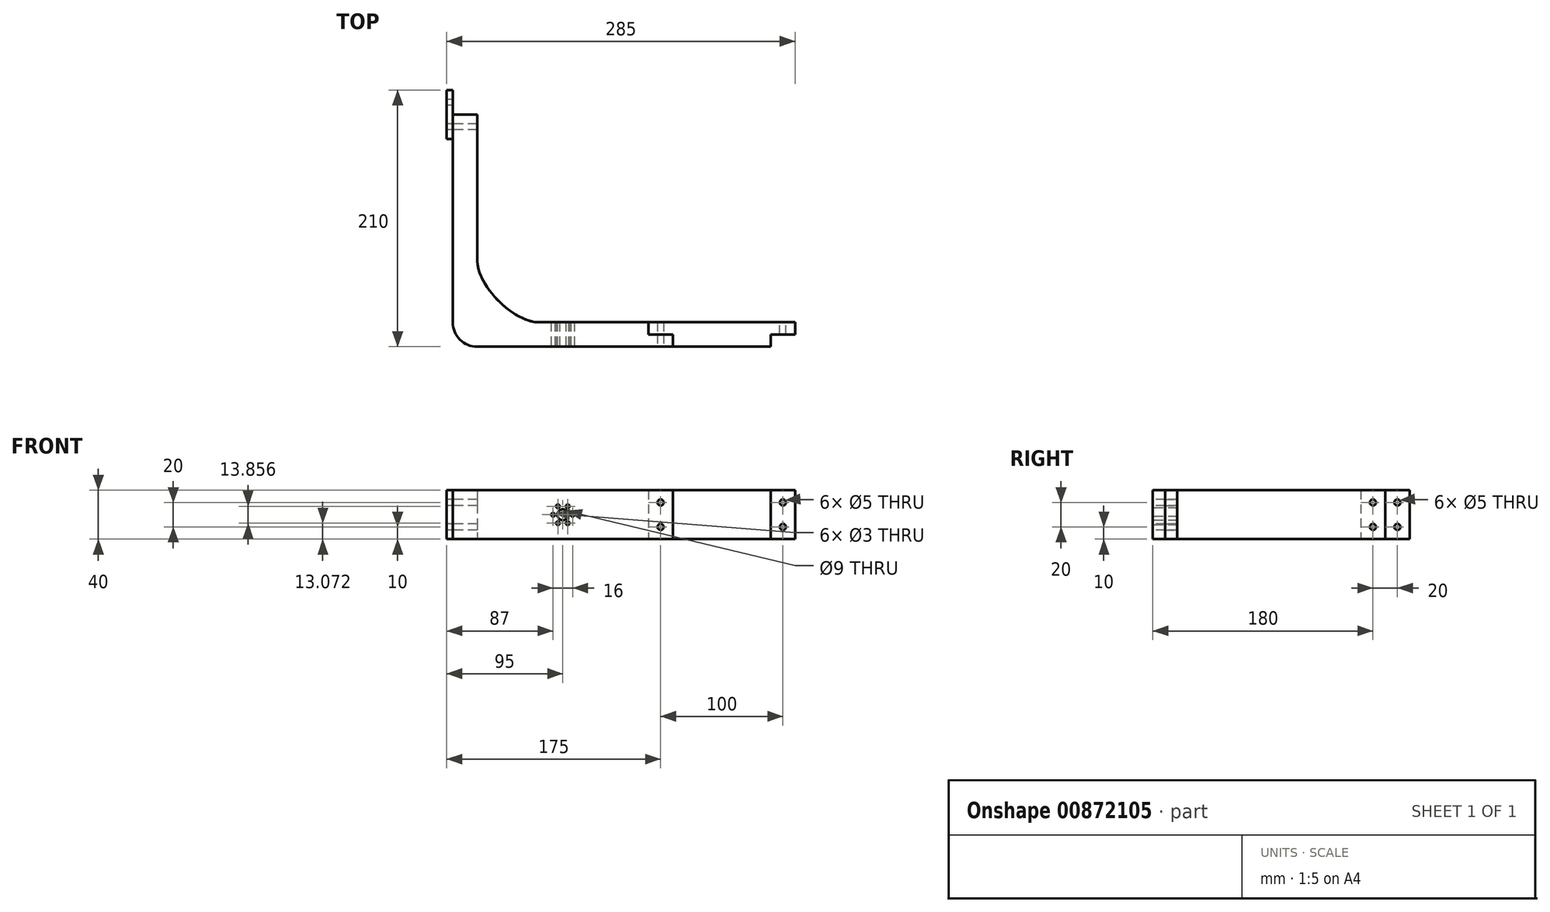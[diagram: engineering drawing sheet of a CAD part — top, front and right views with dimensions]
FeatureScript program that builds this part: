
annotation { "Feature Type Name" : "Feature", "Feature Type Description" : "" }
export const myFeature = defineFeature(function(context is Context, id is Id, definition is map)
    precondition{}
    {
        {
            var Q0;
            Q0=qCreatedBy(makeId("Top.planeOp"),FACE);
            var sketch = newSketch(context, id + "F0", { "sketchPlane" : qUnion([Q0])});
            skLineSegment(sketch, "E0.bottom", {"start": v(0, 0) * mm, "end": v(160, 0) * mm});
            skLineSegment(sketch, "E1", {"start": v(0, 0) * mm, "end": v(-20, 0) * mm});
            skLineSegment(sketch, "E2", {"start": v(-20, 0) * mm, "end": v(-20, 190) * mm});
            skLineSegment(sketch, "E3", {"start": v(160, 0) * mm, "end": v(160, 10) * mm});
            skLineSegment(sketch, "E4", {"start": v(160, 10) * mm, "end": v(140, 10) * mm});
            skLineSegment(sketch, "E5", {"start": v(-20, 190) * mm, "end": v(0, 190) * mm});
            skLineSegment(sketch, "E6", {"start": v(140, 10) * mm, "end": v(140, 20) * mm});
            skLineSegment(sketch, "E7", {"start": v(140, 20) * mm, "end": v(0, 20) * mm});
            skLineSegment(sketch, "E8", {"start": v(0, 20) * mm, "end": v(0, 190) * mm});
            skLineSegment(sketch, "E9", {"start": v(140, 20) * mm, "end": v(260, 20) * mm});
            skLineSegment(sketch, "E10", {"start": v(260, 20) * mm, "end": v(260, 10) * mm});
            skLineSegment(sketch, "E11", {"start": v(260, 10) * mm, "end": v(240, 10) * mm});
            skLineSegment(sketch, "E12", {"start": v(240, 10) * mm, "end": v(240, 0) * mm});
            skLineSegment(sketch, "E13", {"start": v(240, 0) * mm, "end": v(160, 0) * mm});
            skLineSegment(sketch, "E14", {"start": v(-20, 170) * mm, "end": v(-25, 170) * mm});
            skLineSegment(sketch, "E15", {"start": v(-25, 210) * mm, "end": v(-20, 210) * mm});
            skLineSegment(sketch, "E16", {"start": v(-20, 210) * mm, "end": v(-20, 190) * mm});
            skLineSegment(sketch, "E17", {"start": v(-20, 190) * mm, "end": v(-25, 190) * mm, "construction": true});
            skLineSegment(sketch, "E18", {"start": v(-25, 190) * mm, "end": v(-25, 170) * mm});
            skLineSegment(sketch, "E19", {"start": v(-25, 190) * mm, "end": v(-25, 210) * mm});
            skSolve(sketch);
        }
        {
            assignVariable(context, id + "F1", {"name" : "crossHeight", "anyValue" : 40});
        }
        {
            assignVariable(context, id + "F2", {"name" : "cornerHeight", "anyValue" : 40});
        }
        {
            var Q0;
            Q0=makeQuery(id+"F0.imprint","IMPRINT",FACE,{"disambiguationData":[TD([[makeQuery(id+"F0.imprint","IMPRINT",EDGE,{"derivedFrom":sQuery(id+"F0.wireOp",EDGE,"E0.bottom")}),1.0]])]});
            var Q1;
            {var subQ3=sQuery(id+"F0.wireOp",EDGE,"CQL2Ox1S-EhyD-aaeQ-WZRt-JZaB7pT3YKKC");Q1=makeQuery(id+"F0.imprint","IMPRINT",FACE,{"disambiguationData":[TD([[makeQuery(id+"F0.imprint","IMPRINT",EDGE,{"derivedFrom":subQ3}),-1.0]])]});}
            extrude(context, id + "F3", {"entities" : qUnion([Q0, Q1]), "depth" : (getVariable(context, 'cornerHeight')) * mm, "offsetDistance" : 25 * mm});
        }
        {
            var Q0;
            Q0=makeQuery(id+"F3.opExtrude","SWEPT_FACE",FACE,{"disambiguationData":[OSD([sQuery(id+"F0.wireOp",EDGE,"E0.bottom")])]});
            var sketch = newSketch(context, id + "F4", { "sketchPlane" : qUnion([Q0])});
            skCircle(sketch, "E20", {"center": v(70, 20) * mm, "radius": 4.5 * mm});
            skPoint(sketch, "E21", {"position": v(62, 20) * mm});
            skCircle(sketch, "E22", {"center": v(62, 20) * mm, "radius": 1.5 * mm});
            skCircle(sketch, "E23.1.0", {"center": v(66, 13.07) * mm, "radius": 1.5 * mm});
            skCircle(sketch, "E23.2.0", {"center": v(74, 13.07) * mm, "radius": 1.5 * mm});
            skCircle(sketch, "E23.3.0", {"center": v(78, 20) * mm, "radius": 1.5 * mm});
            skCircle(sketch, "E23.4.0", {"center": v(74, 26.93) * mm, "radius": 1.5 * mm});
            skCircle(sketch, "E23.5.0", {"center": v(66, 26.93) * mm, "radius": 1.5 * mm});
            skLineSegment(sketch, "E24.0", {"start": v(160, 40) * mm, "end": v(160, 40) * mm});
            skLineSegment(sketch, "E25", {"start": v(150, 40) * mm, "end": v(150, 30) * mm, "construction": true});
            skCircle(sketch, "E26", {"center": v(150, 30) * mm, "radius": 2.5 * mm});
            skLineSegment(sketch, "E27", {"start": v(150, 0) * mm, "end": v(150, 10) * mm, "construction": true});
            skCircle(sketch, "E28", {"center": v(150, 10) * mm, "radius": 2.5 * mm});
            skLineSegment(sketch, "E29.0", {"start": v(160, 40) * mm, "end": v(140, 40) * mm, "construction": true});
            skLineSegment(sketch, "E30", {"start": v(62, 20) * mm, "end": v(70, 20) * mm, "construction": true});
            skPoint(sketch, "E31.0", {"position": v(0, 40) * mm});
            skLineSegment(sketch, "E32", {"start": v(70, 20) * mm, "end": v(70, 40) * mm, "construction": true});
            skLineSegment(sketch, "E33", {"start": v(70, 20) * mm, "end": v(70, 0) * mm, "construction": true});
            skSolve(sketch);
        }
        {
            var Q0;
            Q0=makeQuery(id+"F3.opExtrude","SWEPT_FACE",FACE,{"disambiguationData":[OSD([sQuery(id+"F0.wireOp",EDGE,"E2")])]});
            var sketch = newSketch(context, id + "F5", { "sketchPlane" : qUnion([Q0])});
            skLineSegment(sketch, "E34.0", {"start": v(-170, 40) * mm, "end": v(-190, 40) * mm, "construction": true});
            skLineSegment(sketch, "E35", {"start": v(-180, 40) * mm, "end": v(-180, 30) * mm, "construction": true});
            skCircle(sketch, "E36", {"center": v(-180, 30) * mm, "radius": 2.5 * mm});
            skLineSegment(sketch, "E37", {"start": v(-180, 0) * mm, "end": v(-180, 10) * mm, "construction": true});
            skCircle(sketch, "E38", {"center": v(-180, 10) * mm, "radius": 2.5 * mm});
            skSolve(sketch);
        }
        {
            var Q0;
            Q0=makeQuery(id+"F5.imprint","IMPRINT",FACE,{"disambiguationData":[TD([[makeQuery(id+"F5.imprint","IMPRINT",EDGE,{"derivedFrom":sQuery(id+"F5.wireOp",EDGE,"E36")}),1.0]])]});
            var Q1;
            Q1=makeQuery(id+"F5.imprint","IMPRINT",FACE,{"disambiguationData":[TD([[makeQuery(id+"F5.imprint","IMPRINT",EDGE,{"derivedFrom":sQuery(id+"F5.wireOp",EDGE,"E38")}),1.0]])]});
            extrude(context, id + "F6", {"entities" : qUnion([Q0, Q1]), "operationType" : NewBodyOperationType.REMOVE, "endBound" : BoundingType.THROUGH_ALL, "oppositeDirection" : true, "depth" : 25 * mm, "offsetDistance" : 25 * mm});
        }
        {
            var Q0;
            Q0=makeQuery(id+"F0.imprint","IMPRINT",FACE,{"disambiguationData":[TD([[makeQuery(id+"F0.imprint","IMPRINT",EDGE,{"derivedFrom":sQuery(id+"F0.wireOp",EDGE,"E3")}),-1.0]])]});
            extrude(context, id + "F7", {"entities" : qUnion([Q0]), "depth" : (getVariable(context, 'crossHeight')) * mm, "offsetDistance" : 25 * mm});
        }
        {
            var Q0;
            Q0=makeQuery(id+"F4.imprint","IMPRINT",FACE,{"disambiguationData":[TD([[makeQuery(id+"F4.imprint","IMPRINT",EDGE,{"derivedFrom":sQuery(id+"F4.wireOp",EDGE,"E20")}),1.0]])]});
            var Q1;
            Q1=makeQuery(id+"F4.imprint","IMPRINT",FACE,{"disambiguationData":[TD([[makeQuery(id+"F4.imprint","IMPRINT",EDGE,{"derivedFrom":sQuery(id+"F4.wireOp",EDGE,"E23.1.0")}),1.0]])]});
            var Q2;
            Q2=makeQuery(id+"F4.imprint","IMPRINT",FACE,{"disambiguationData":[TD([[makeQuery(id+"F4.imprint","IMPRINT",EDGE,{"derivedFrom":sQuery(id+"F4.wireOp",EDGE,"E22")}),1.0]])]});
            var Q3;
            Q3=makeQuery(id+"F4.imprint","IMPRINT",FACE,{"disambiguationData":[TD([[makeQuery(id+"F4.imprint","IMPRINT",EDGE,{"derivedFrom":sQuery(id+"F4.wireOp",EDGE,"E23.5.0")}),1.0]])]});
            var Q4;
            Q4=makeQuery(id+"F4.imprint","IMPRINT",FACE,{"disambiguationData":[TD([[makeQuery(id+"F4.imprint","IMPRINT",EDGE,{"derivedFrom":sQuery(id+"F4.wireOp",EDGE,"E23.4.0")}),1.0]])]});
            var Q5;
            Q5=makeQuery(id+"F4.imprint","IMPRINT",FACE,{"disambiguationData":[TD([[makeQuery(id+"F4.imprint","IMPRINT",EDGE,{"derivedFrom":sQuery(id+"F4.wireOp",EDGE,"E23.3.0")}),1.0]])]});
            var Q6;
            Q6=makeQuery(id+"F4.imprint","IMPRINT",FACE,{"disambiguationData":[TD([[makeQuery(id+"F4.imprint","IMPRINT",EDGE,{"derivedFrom":sQuery(id+"F4.wireOp",EDGE,"E23.2.0")}),1.0]])]});
            var Q7;
            Q7=makeQuery(id+"F4.imprint","IMPRINT",FACE,{"disambiguationData":[TD([[makeQuery(id+"F4.imprint","IMPRINT",EDGE,{"derivedFrom":sQuery(id+"F4.wireOp",EDGE,"5a667269-1d9d-4c14-9df4-f803b36f7a04.1.0")}),1.0]])]});
            var Q8;
            Q8=makeQuery(id+"F4.imprint","IMPRINT",FACE,{"disambiguationData":[TD([[makeQuery(id+"F4.imprint","IMPRINT",EDGE,{"derivedFrom":sQuery(id+"F4.wireOp",EDGE,"9fac3a3e-27b1-4231-b030-443598fcf0e1")}),1.0]])]});
            var Q9;
            Q9=makeQuery(id+"F4.imprint","IMPRINT",FACE,{"disambiguationData":[TD([[makeQuery(id+"F4.imprint","IMPRINT",EDGE,{"derivedFrom":sQuery(id+"F4.wireOp",EDGE,"5a667269-1d9d-4c14-9df4-f803b36f7a04.5.0")}),1.0]])]});
            var Q10;
            Q10=makeQuery(id+"F4.imprint","IMPRINT",FACE,{"disambiguationData":[TD([[makeQuery(id+"F4.imprint","IMPRINT",EDGE,{"derivedFrom":sQuery(id+"F4.wireOp",EDGE,"5a667269-1d9d-4c14-9df4-f803b36f7a04.4.0")}),1.0]])]});
            var Q11;
            Q11=makeQuery(id+"F4.imprint","IMPRINT",FACE,{"disambiguationData":[TD([[makeQuery(id+"F4.imprint","IMPRINT",EDGE,{"derivedFrom":sQuery(id+"F4.wireOp",EDGE,"5a667269-1d9d-4c14-9df4-f803b36f7a04.3.0")}),1.0]])]});
            var Q12;
            Q12=makeQuery(id+"F4.imprint","IMPRINT",FACE,{"disambiguationData":[TD([[makeQuery(id+"F4.imprint","IMPRINT",EDGE,{"derivedFrom":sQuery(id+"F4.wireOp",EDGE,"5a667269-1d9d-4c14-9df4-f803b36f7a04.2.0")}),1.0]])]});
            var Q13;
            Q13=makeQuery(id+"F4.imprint","IMPRINT",FACE,{"disambiguationData":[TD([[makeQuery(id+"F4.imprint","IMPRINT",EDGE,{"derivedFrom":sQuery(id+"F4.wireOp",EDGE,"db13373e-4026-48fc-84c4-6d5f9d0bf7ed")}),1.0]])]});
            var Q14;
            Q14=makeQuery(id+"F4.imprint","IMPRINT",FACE,{"disambiguationData":[TD([[makeQuery(id+"F4.imprint","IMPRINT",EDGE,{"derivedFrom":sQuery(id+"F4.wireOp",EDGE,"12868623-197d-4bdd-8fc8-ae995a3a8a75.2.0")}),1.0]])]});
            var Q15;
            Q15=makeQuery(id+"F4.imprint","IMPRINT",FACE,{"disambiguationData":[TD([[makeQuery(id+"F4.imprint","IMPRINT",EDGE,{"derivedFrom":sQuery(id+"F4.wireOp",EDGE,"7076aaa0-8fd6-4c28-89e9-1ae1bcceeb62")}),1.0]])]});
            var Q16;
            Q16=makeQuery(id+"F4.imprint","IMPRINT",FACE,{"disambiguationData":[TD([[makeQuery(id+"F4.imprint","IMPRINT",EDGE,{"derivedFrom":sQuery(id+"F4.wireOp",EDGE,"12868623-197d-4bdd-8fc8-ae995a3a8a75.1.0")}),1.0]])]});
            var Q17;
            Q17=makeQuery(id+"F4.imprint","IMPRINT",FACE,{"disambiguationData":[TD([[makeQuery(id+"F4.imprint","IMPRINT",EDGE,{"derivedFrom":sQuery(id+"F4.wireOp",EDGE,"043e2786-b5b6-42c8-8913-0fcca367663f")}),1.0]])]});
            var Q18;
            Q18=makeQuery(id+"F4.imprint","IMPRINT",FACE,{"disambiguationData":[TD([[makeQuery(id+"F4.imprint","IMPRINT",EDGE,{"derivedFrom":sQuery(id+"F4.wireOp",EDGE,"12868623-197d-4bdd-8fc8-ae995a3a8a75.5.0")}),1.0]])]});
            var Q19;
            Q19=makeQuery(id+"F4.imprint","IMPRINT",FACE,{"disambiguationData":[TD([[makeQuery(id+"F4.imprint","IMPRINT",EDGE,{"derivedFrom":sQuery(id+"F4.wireOp",EDGE,"12868623-197d-4bdd-8fc8-ae995a3a8a75.4.0")}),1.0]])]});
            var Q20;
            Q20=makeQuery(id+"F4.imprint","IMPRINT",FACE,{"disambiguationData":[TD([[makeQuery(id+"F4.imprint","IMPRINT",EDGE,{"derivedFrom":sQuery(id+"F4.wireOp",EDGE,"12868623-197d-4bdd-8fc8-ae995a3a8a75.3.0")}),1.0]])]});
            var Q21;
            Q21=makeQuery(id+"F4.imprint","IMPRINT",FACE,{"disambiguationData":[TD([[makeQuery(id+"F4.imprint","IMPRINT",EDGE,{"derivedFrom":sQuery(id+"F4.wireOp",EDGE,"E26")}),1.0]])]});
            var Q22;
            Q22=makeQuery(id+"F4.imprint","IMPRINT",FACE,{"disambiguationData":[TD([[makeQuery(id+"F4.imprint","IMPRINT",EDGE,{"derivedFrom":sQuery(id+"F4.wireOp",EDGE,"E28")}),1.0]])]});
            extrude(context, id + "F8", {"entities" : qUnion([Q0, Q1, Q2, Q3, Q4, Q5, Q6, Q7, Q8, Q9, Q10, Q11, Q12, Q13, Q14, Q15, Q16, Q17, Q18, Q19, Q20, Q21, Q22]), "operationType" : NewBodyOperationType.REMOVE, "endBound" : BoundingType.THROUGH_ALL, "oppositeDirection" : true, "depth" : 25 * mm, "offsetDistance" : 25 * mm});
        }
        {
            var Q0;
            Q0=makeQuery(id+"F7.opExtrude","SWEPT_FACE",FACE,{"disambiguationData":[OSD([sQuery(id+"F0.wireOp",EDGE,"E9")])]});
            var sketch = newSketch(context, id + "F9", { "sketchPlane" : qUnion([Q0])});
            skLineSegment(sketch, "E39.0", {"start": v(-240, 40) * mm, "end": v(-260, 40) * mm, "construction": true});
            skLineSegment(sketch, "E40", {"start": v(-250, 40) * mm, "end": v(-250, 30) * mm, "construction": true});
            skCircle(sketch, "E41", {"center": v(-250, 30) * mm, "radius": 2.5 * mm});
            skLineSegment(sketch, "E42", {"start": v(-250, 0) * mm, "end": v(-250, 10) * mm, "construction": true});
            skCircle(sketch, "E43", {"center": v(-250, 10) * mm, "radius": 2.5 * mm});
            skPoint(sketch, "E44.0", {"position": v(-240, 40) * mm});
            skSolve(sketch);
        }
        {
            var Q0;
            Q0=makeQuery(id+"F9.imprint","IMPRINT",FACE,{"disambiguationData":[TD([[makeQuery(id+"F9.imprint","IMPRINT",EDGE,{"derivedFrom":sQuery(id+"F9.wireOp",EDGE,"E41")}),1.0]])]});
            var Q1;
            Q1=makeQuery(id+"F9.imprint","IMPRINT",FACE,{"disambiguationData":[TD([[makeQuery(id+"F9.imprint","IMPRINT",EDGE,{"derivedFrom":sQuery(id+"F9.wireOp",EDGE,"E43")}),1.0]])]});
            extrude(context, id + "F10", {"entities" : qUnion([Q0, Q1]), "operationType" : NewBodyOperationType.REMOVE, "endBound" : BoundingType.THROUGH_ALL, "oppositeDirection" : true, "depth" : 25 * mm, "offsetDistance" : 25 * mm});
        }
        {
            var Q0;
            Q0=makeQuery(id+"F3.opExtrude","SWEPT_EDGE",EDGE,{"disambiguationData":[OSD([sQuery(id+"F0.wireOp",EDGE,"E7"),sQuery(id+"F0.wireOp",EDGE,"E8")])]});
            fillet(context, id + "F11", {"entities" : qUnion([Q0]), "radius" : 50 * mm, "rho" : .3, "crossSection" : FilletCrossSection.CONIC, "allowEdgeOverflow" : false});
        }
        {
            var Q0;
            Q0=makeQuery(id+"F3.opExtrude","SWEPT_EDGE",EDGE,{"disambiguationData":[OSD([sQuery(id+"F0.wireOp",EDGE,"E1"),sQuery(id+"F0.wireOp",EDGE,"E2")])]});
            fillet(context, id + "F12", {"entities" : qUnion([Q0]), "radius" : 20 * mm, "tangentPropagation" : true, "allowEdgeOverflow" : false});
        }
        {
            var Q0;
            {var subQ1=sQuery(id+"F0.wireOp",EDGE,"E14");Q0=makeQuery(id+"F0.imprint","IMPRINT",FACE,{"disambiguationData":[TD([[makeQuery(id+"F0.imprint","IMPRINT",EDGE,{"derivedFrom":subQ1}),-1.0]])]});}
            extrude(context, id + "F13", {"entities" : qUnion([Q0]), "depth" : (getVariable(context, 'cornerHeight')) * mm, "offsetDistance" : 25 * mm});
        }
        {
            var Q0;
            Q0=makeQuery(id+"F13.opExtrude","SWEPT_FACE",FACE,{"disambiguationData":[OSD([sQuery(id+"F0.wireOp",EDGE,"E18"),sQuery(id+"F0.wireOp",EDGE,"E19")])]});
            var sketch = newSketch(context, id + "F14", { "sketchPlane" : qUnion([Q0])});
            skLineSegment(sketch, "E45.0", {"start": v(-190, 40) * mm, "end": v(-210, 40) * mm, "construction": true});
            skLineSegment(sketch, "E46", {"start": v(-200, 40) * mm, "end": v(-200, 30) * mm, "construction": true});
            skCircle(sketch, "E47", {"center": v(-200, 30) * mm, "radius": 2.5 * mm});
            skLineSegment(sketch, "E48", {"start": v(-200, 0) * mm, "end": v(-200, 10) * mm, "construction": true});
            skCircle(sketch, "E49", {"center": v(-200, 10) * mm, "radius": 2.5 * mm});
            skLineSegment(sketch, "E50.0", {"start": v(-170, 40) * mm, "end": v(-190, 40) * mm, "construction": true});
            skLineSegment(sketch, "E51", {"start": v(-180, 40) * mm, "end": v(-180, 30) * mm, "construction": true});
            skCircle(sketch, "E52", {"center": v(-180, 30) * mm, "radius": 2.5 * mm});
            skLineSegment(sketch, "E53", {"start": v(-180, 0) * mm, "end": v(-180, 10) * mm, "construction": true});
            skCircle(sketch, "E54", {"center": v(-180, 10) * mm, "radius": 2.5 * mm});
            skSolve(sketch);
        }
        {
            var Q0;
            Q0=makeQuery(id+"F14.imprint","IMPRINT",FACE,{"disambiguationData":[TD([[makeQuery(id+"F14.imprint","IMPRINT",EDGE,{"derivedFrom":sQuery(id+"F14.wireOp",EDGE,"E47")}),1.0]])]});
            var Q1;
            Q1=makeQuery(id+"F14.imprint","IMPRINT",FACE,{"disambiguationData":[TD([[makeQuery(id+"F14.imprint","IMPRINT",EDGE,{"derivedFrom":sQuery(id+"F14.wireOp",EDGE,"E52")}),1.0]])]});
            var Q2;
            Q2=makeQuery(id+"F14.imprint","IMPRINT",FACE,{"disambiguationData":[TD([[makeQuery(id+"F14.imprint","IMPRINT",EDGE,{"derivedFrom":sQuery(id+"F14.wireOp",EDGE,"E54")}),1.0]])]});
            var Q3;
            Q3=makeQuery(id+"F14.imprint","IMPRINT",FACE,{"disambiguationData":[TD([[makeQuery(id+"F14.imprint","IMPRINT",EDGE,{"derivedFrom":sQuery(id+"F14.wireOp",EDGE,"E49")}),1.0]])]});
            extrude(context, id + "F15", {"entities" : qUnion([Q0, Q1, Q2, Q3]), "operationType" : NewBodyOperationType.REMOVE, "endBound" : BoundingType.THROUGH_ALL, "oppositeDirection" : true, "depth" : 25 * mm, "offsetDistance" : 25 * mm});
        }
    });
